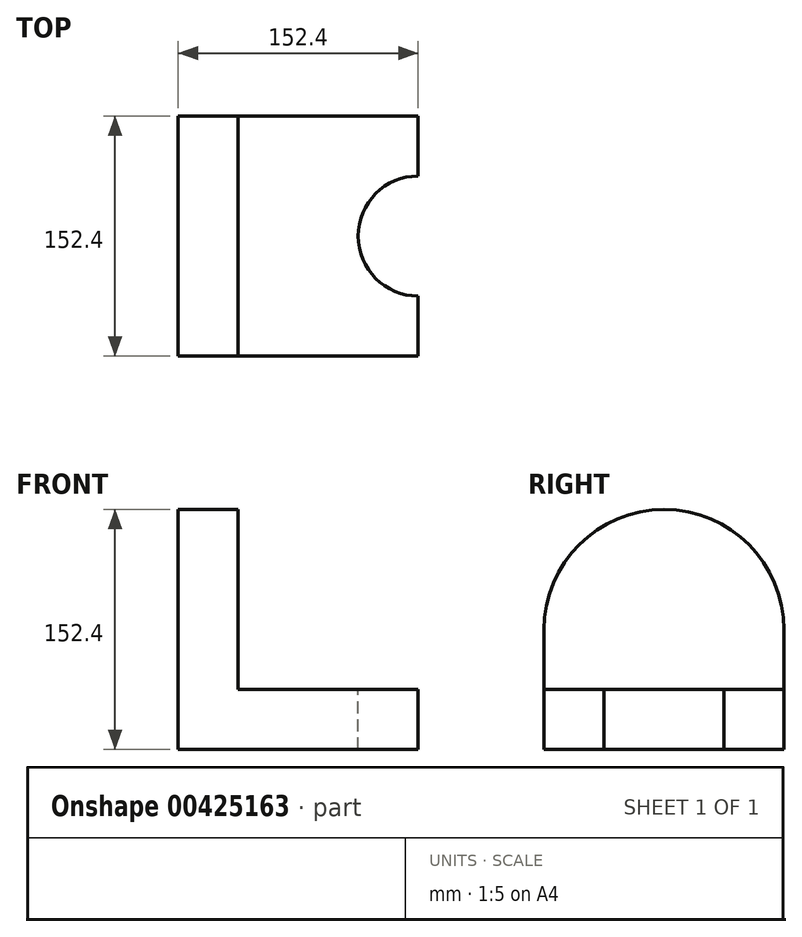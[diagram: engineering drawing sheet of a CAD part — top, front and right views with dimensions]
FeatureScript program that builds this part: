
annotation { "Feature Type Name" : "Feature", "Feature Type Description" : "" }
export const myFeature = defineFeature(function(context is Context, id is Id, definition is map)
    precondition{}
    {
        {
            var Q0;
            Q0=qCreatedBy(makeId("Front.planeOp"),FACE);
            var sketch = newSketch(context, id + "F0", { "sketchPlane" : qUnion([Q0])});
            skLineSegment(sketch, "E0.bottom", {"start": v(0, 0) * mm, "end": v(152.4, 0) * mm});
            skLineSegment(sketch, "E0.top", {"start": v(0, 152.4) * mm, "end": v(152.4, 152.4) * mm});
            skLineSegment(sketch, "E0.left", {"start": v(0, 0) * mm, "end": v(0, 152.4) * mm});
            skLineSegment(sketch, "E0.right", {"start": v(152.4, 0) * mm, "end": v(152.4, 152.4) * mm});
            skSolve(sketch);
        }
        {
            var Q0;
            Q0=qSketchRegion(id+"F0",true);
            extrude(context, id + "F1", {"entities" : qUnion([Q0]), "depth" : 152.4 * mm});
        }
        {
            var Q0;
            Q0=makeQuery(id+"F1.opExtrude","CAP_FACE",FACE,{"disambiguationData":[OSD([sQuery(id+"F0.wireOp",EDGE,"E0.bottom"),sQuery(id+"F0.wireOp",EDGE,"E0.top"),sQuery(id+"F0.wireOp",EDGE,"E0.left"),sQuery(id+"F0.wireOp",EDGE,"E0.right")])],"isStart":false});
            var sketch = newSketch(context, id + "F2", { "sketchPlane" : qUnion([Q0])});
            skLineSegment(sketch, "E1.bottom", {"start": v(152.4, 152.4) * mm, "end": v(38.1, 152.4) * mm});
            skLineSegment(sketch, "E1.top", {"start": v(152.4, 38.1) * mm, "end": v(38.1, 38.1) * mm});
            skLineSegment(sketch, "E1.left", {"start": v(152.4, 152.4) * mm, "end": v(152.4, 38.1) * mm});
            skLineSegment(sketch, "E1.right", {"start": v(38.1, 152.4) * mm, "end": v(38.1, 38.1) * mm});
            skSolve(sketch);
        }
        {
            var Q0;
            Q0=qSketchRegion(id+"F2",true);
            extrude(context, id + "F3", {"entities" : qUnion([Q0]), "operationType" : NewBodyOperationType.REMOVE, "oppositeDirection" : true, "depth" : 152.4 * mm});
        }
        {
            var Q0;
            Q0=makeQuery(id+"F3.boolean.opBoolean","COPY",FACE,{"derivedFrom":makeQuery(id+"F3.opExtrude","SWEPT_FACE",FACE,{"disambiguationData":[OSD([sQuery(id+"F2.wireOp",EDGE,"E1.top")])]})});
            var sketch = newSketch(context, id + "F4", { "sketchPlane" : qUnion([Q0])});
            skPoint(sketch, "E2", {"position": v(152.4, -76.2) * mm});
            skCircle(sketch, "E3", {"center": v(152.4, -76.2) * mm, "radius": 38.1 * mm});
            skSolve(sketch);
        }
        {
            var Q0;
            Q0 = qSketchRegion(id + "F4", true);
            extrude(context, id + "F5", {"entities" : qUnion([Q0]), "operationType" : NewBodyOperationType.REMOVE, "oppositeDirection" : true, "depth" : 76.2 * mm});
        }
        {
            var Q0;
            Q0=makeQuery(id+"F3.boolean.opBoolean","COPY",FACE,{"derivedFrom":makeQuery(id+"F3.opExtrude","SWEPT_FACE",FACE,{"disambiguationData":[OSD([sQuery(id+"F2.wireOp",EDGE,"E1.right")])]})});
            var sketch = newSketch(context, id + "F6", { "sketchPlane" : qUnion([Q0])});
            skLineSegment(sketch, "E4.bottom", {"start": v(-152.4, 152.4) * mm, "end": v(0, 152.4) * mm});
            skLineSegment(sketch, "E4.left", {"start": v(-152.4, 152.4) * mm, "end": v(-152.4, 76.2) * mm});
            skLineSegment(sketch, "E4.right", {"start": v(0, 152.4) * mm, "end": v(0, 76.2) * mm});
            skLineSegment(sketch, "E5", {"start": v(-152.4, 76.2) * mm, "end": v(0, 76.2) * mm, "construction": true});
            skPoint(sketch, "E6", {"position": v(-76.2, 76.2) * mm});
            skArc(sketch, "E7", {"start": v(-152.4, 76.2) * mm, "mid": v(-76.2, 152.4) * mm, "end": v(0, 76.2) * mm});
            skPoint(sketch, "E8", {"position": v(-76.2, 152.4) * mm});
            skSolve(sketch);
        }
        {
            var Q0;
            {var subQ0=sQuery(id+"F6.wireOp",EDGE,"E4.left");Q0=makeQuery(id+"F6.imprint","IMPRINT",FACE,{"disambiguationData":[TD([[makeQuery(id+"F6.imprint","IMPRINT",EDGE,{"derivedFrom":subQ0}),1.0]])]});}
            var Q1;
            {var subQ0=sQuery(id+"F6.wireOp",EDGE,"E4.right");Q1=makeQuery(id+"F6.imprint","IMPRINT",FACE,{"disambiguationData":[TD([[makeQuery(id+"F6.imprint","IMPRINT",EDGE,{"derivedFrom":subQ0}),-1.0]])]});}
            extrude(context, id + "F7", {"entities" : qUnion([Q0, Q1]), "operationType" : NewBodyOperationType.REMOVE, "oppositeDirection" : true, "depth" : 304.8 * mm});
        }
    });
